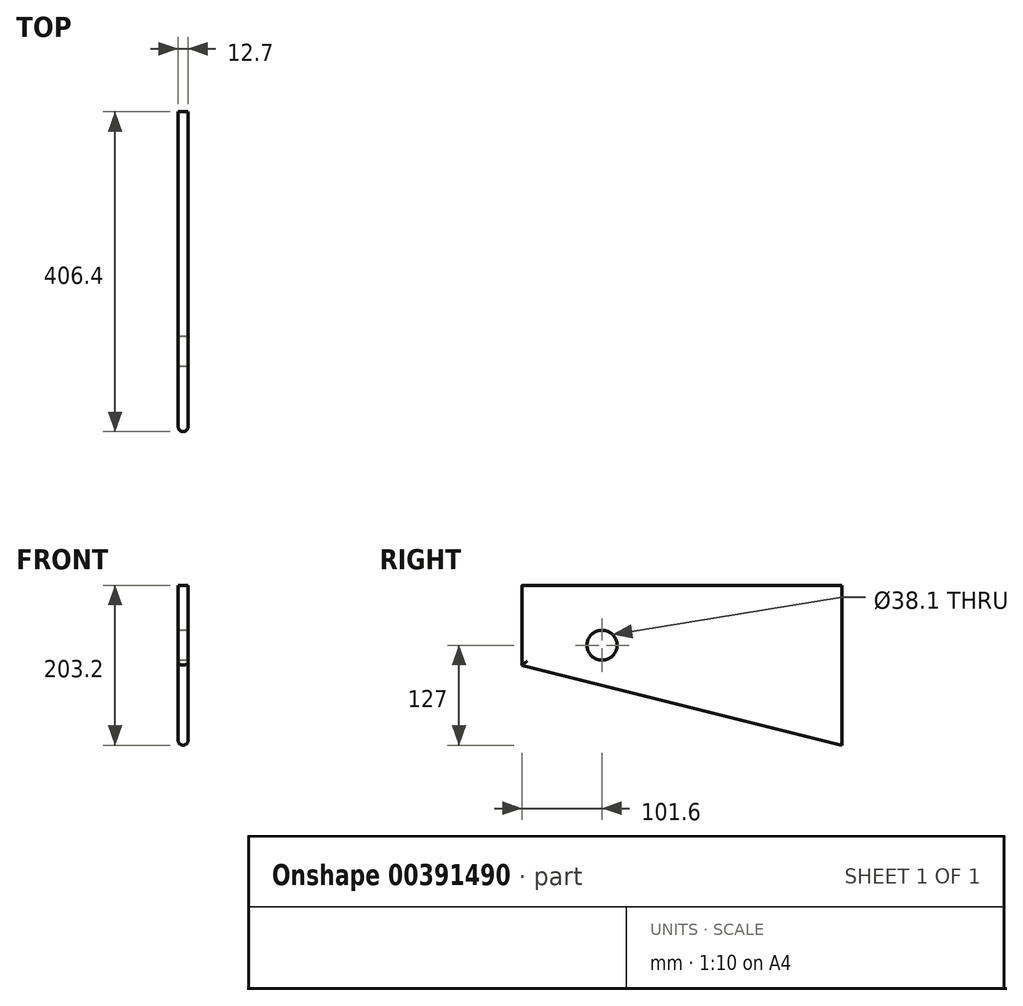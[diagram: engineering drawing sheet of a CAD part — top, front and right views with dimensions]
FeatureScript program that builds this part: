
annotation { "Feature Type Name" : "Feature", "Feature Type Description" : "" }
export const myFeature = defineFeature(function(context is Context, id is Id, definition is map)
    precondition{}
    {
        {
            var Q0;
            Q0=qCreatedBy(makeId("Right.planeOp"),FACE);
            var sketch = newSketch(context, id + "F0", { "sketchPlane" : qUnion([Q0])});
            skLineSegment(sketch, "E0.bottom", {"start": v(0, 0) * mm, "end": v(406.4, 0) * mm});
            skLineSegment(sketch, "E0.top", {"start": v(0, -101.6) * mm, "end": v(406.4, -203.2) * mm});
            skLineSegment(sketch, "E0.left", {"start": v(0, 0) * mm, "end": v(0, -101.6) * mm});
            skLineSegment(sketch, "E0.right", {"start": v(406.4, 0) * mm, "end": v(406.4, -203.2) * mm});
            skCircle(sketch, "E1", {"center": v(101.6, -76.2) * mm, "radius": 19.05 * mm});
            skSolve(sketch);
        }
        {
            var Q0;
            Q0 = qSketchRegion(id + "F0", true);
            extrude(context, id + "F1", {"entities" : qUnion([Q0]), "depth" : 12.7 * mm, "symmetric" : true});
        }
        {
            var Q0;
            Q0=makeQuery(id+"F1.opExtrude","CAP_EDGE",EDGE,{"disambiguationData":[OSD([sQuery(id+"F0.wireOp",EDGE,"E0.top")])],"isStart":true});
            var Q1;
            Q1=makeQuery(id+"F1.opExtrude","CAP_EDGE",EDGE,{"disambiguationData":[OSD([sQuery(id+"F0.wireOp",EDGE,"E0.top")])],"isStart":false});
            var Q2;
            Q2=makeQuery(id+"F1.opExtrude","CAP_EDGE",EDGE,{"disambiguationData":[OSD([sQuery(id+"F0.wireOp",EDGE,"E0.left")])],"isStart":false});
            var Q3;
            Q3=makeQuery(id+"F1.opExtrude","CAP_EDGE",EDGE,{"disambiguationData":[OSD([sQuery(id+"F0.wireOp",EDGE,"E0.left")])],"isStart":true});
            fillet(context, id + "F2", {"entities" : qUnion([Q0, Q1, Q2, Q3]), "radius" : 6.35 * mm, "tangentPropagation" : true, "allowEdgeOverflow" : false});
        }
    });
